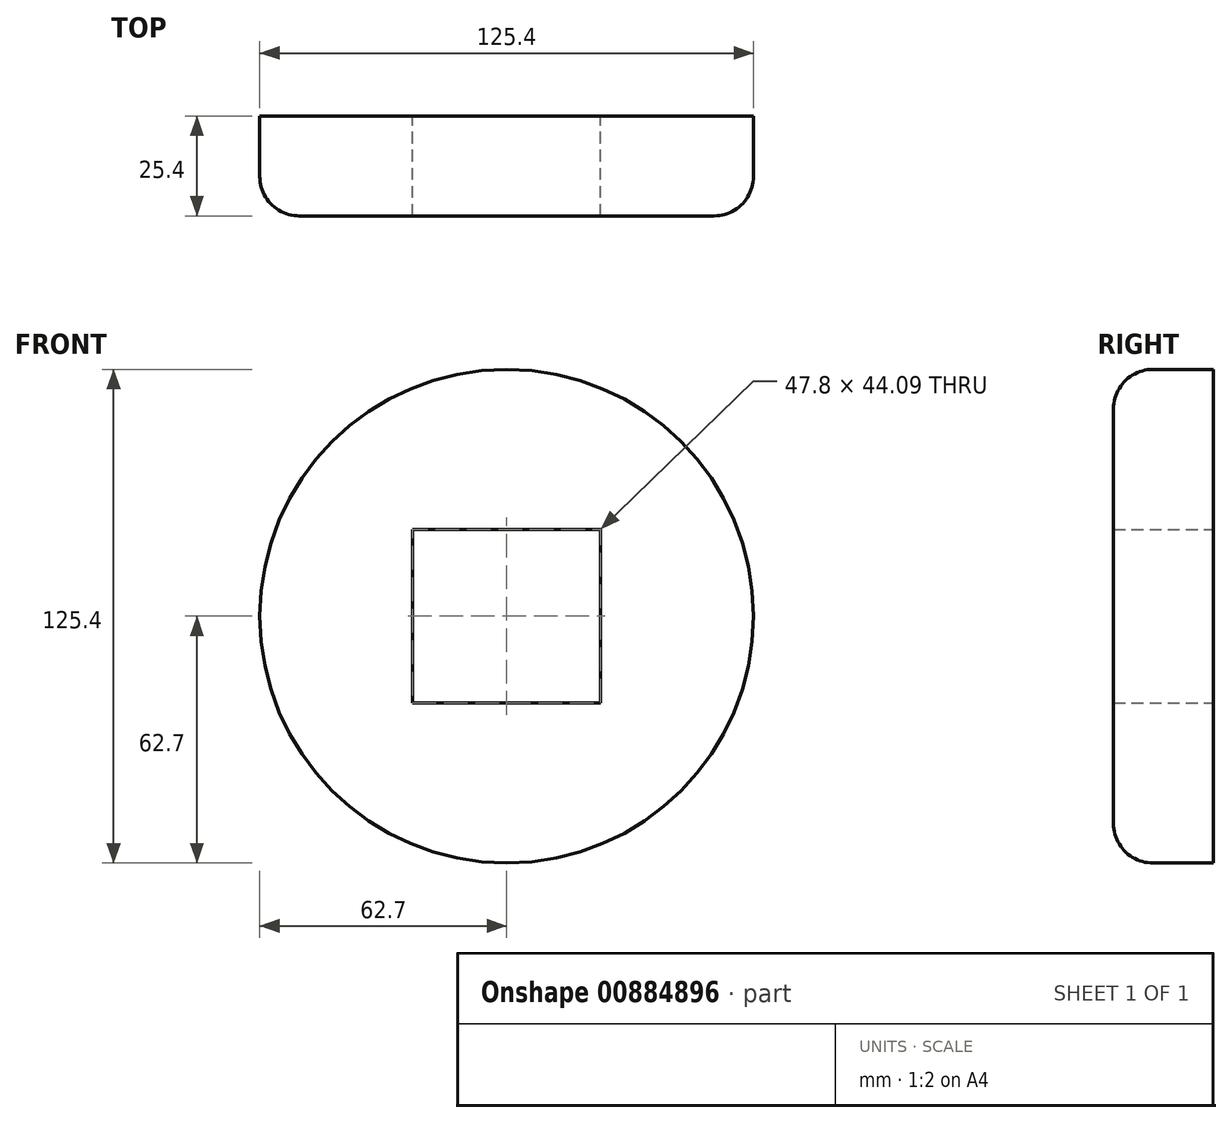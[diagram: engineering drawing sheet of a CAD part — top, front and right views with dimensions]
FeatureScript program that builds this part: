
annotation { "Feature Type Name" : "Feature", "Feature Type Description" : "" }
export const myFeature = defineFeature(function(context is Context, id is Id, definition is map)
    precondition{}
    {
        {
            var Q0;
            Q0=qCreatedBy(makeId("Front.planeOp"),FACE);
            var sketch = newSketch(context, id + "F0", { "sketchPlane" : qUnion([Q0])});
            skCircle(sketch, "E0", {"center": v(0, 0) * mm, "radius": 62.7 * mm});
            skCircle(sketch, "E1", {"center": v(151.44, 0) * mm, "radius": 88.74 * mm});
            skSolve(sketch);
        }
        {
            var Q0;
            Q0=qCreatedBy(makeId("Front.planeOp"),FACE);
            var sketch = newSketch(context, id + "F1", { "sketchPlane" : qUnion([Q0])});
            skLineSegment(sketch, "E2.bottom", {"start": v(23.9, -22.04) * mm, "end": v(-23.9, -22.04) * mm});
            skLineSegment(sketch, "E2.top", {"start": v(23.9, 22.04) * mm, "end": v(-23.9, 22.04) * mm});
            skLineSegment(sketch, "E2.left", {"start": v(23.9, -22.04) * mm, "end": v(23.9, 22.04) * mm});
            skLineSegment(sketch, "E2.right", {"start": v(-23.9, -22.04) * mm, "end": v(-23.9, 22.04) * mm});
            skPoint(sketch, "E2.middle", {"position": v(0, 0) * mm});
            skSolve(sketch);
        }
        {
            var Q0;
            Q0=makeQuery(id+"F0.imprint","IMPRINT",FACE,{"disambiguationData":[TD([[makeQuery(id+"F0.imprint","IMPRINT",EDGE,{"derivedFrom":sQuery(id+"F0.wireOp",EDGE,"E0")}),1.0]])]});
            extrude(context, id + "F2", {"entities" : qUnion([Q0]), "depth" : 25.4 * mm, "offsetDistance" : 25.4 * mm});
        }
        {
            var Q0;
            Q0=makeQuery(id+"F1.imprint","IMPRINT",FACE,{"disambiguationData":[TD([[makeQuery(id+"F1.imprint","IMPRINT",EDGE,{"derivedFrom":sQuery(id+"F1.wireOp",EDGE,"E2.bottom")}),-1.0]])]});
            extrude(context, id + "F3", {"entities" : qUnion([Q0]), "operationType" : NewBodyOperationType.REMOVE, "depth" : 30 * mm, "offsetDistance" : 25 * mm});
        }
        {
            var Q0;
            Q0=makeQuery(id+"F2.opExtrude","CAP_EDGE",EDGE,{"disambiguationData":[OSD([sQuery(id+"F0.wireOp",EDGE,"E0")])],"isStart":false});
            fillet(context, id + "F4", {"entities" : qUnion([Q0]), "radius" : 10 * mm, "tangentPropagation" : true, "allowEdgeOverflow" : false});
        }
    });
